# Revit family: O93 LED 130000 DALI 740 XNB_Unhosted
name_source: partatom
category: Lighting Fixtures
revit_build: Autodesk Revit 2016 (Build: 20161004_0715(x64)
units: mm (PartAtom-declared; Revit-internal decimal feet)

## family parameters
Always vertical = Yes
Cut with Voids When Loaded = No
Light Source = Yes
OmniClass Number = 23.80.70.00
OmniClass Title = Lighting
Part Type = Normal
Room Calculation Point = No
Round Connector Dimension = Use Diameter
Shared = No
Work Plane-Based = No

## types (1)
- O93 LED 130000 DALI 740 XNB_Unhosted
    #Ballast = 3
    Apparent Load = 867 VA
    ArticleNumber = 514084501
    Body Material and Colour = Default
    Color Filter = 16777215
    Description = O93 LED 130000 DALI 740 XNB
    Dimming Lamp Color Temperature Shift = Incandescent Lamp Curve
    EANNo = 8019455840118
    Emit Shape Visible in Rendering = Yes
    Emit from Rectangle Length = 565 mm
    Emit from Rectangle Width = 630 mm
    Expired = 0
    Frequency = 50 Hz
    FrequencyMax = 60 Hz
    Glamox Category = Outdoor
    Glamox Family = O93
    Glamox Mounting = Wall
    GlobalTradeItemNumber = 8019455840118
    Height = 398 mm
    Height2 = 40 mm
    IFC Classification = Light Fixture
    IPClass = 66
    IP_Code = 66
    Lamp = LED
    Length = 674 mm
    LightFixtureMountingType = OTHER
    LightFixturePlacingType = OTHER
    LumLength = 630 mm
    LumWidth = 565 mm
    MFArtNo = 514084501
    MaintenanceFactor = 0
    Manufacturer = Glamox
    Maximum TA = 35
    ModelLabel = O93 LED 130000 DALI 740 XNB
    ModelReference = O93
    NominalFrequencyRange = 50 Hz
    Number of Poles = 1
    Optic = XNB
    Photometric Web File = O93-LED-130000-DALI-740-XNB.ies
    Power Factor = 0.98
    PowerFactor = 98.00%
    RatedVoltage = 220 V
    Specification = Outdoor product, in Aluminium, for Wall/Facade/Pole mounting, impact classification IK8, IP66, light source LED, lumen out 126500lm, ballast type DALI, with light source type CRI>70, 4000K, optic type XNB = extra narrow beam.
    Termination = 5x6 SC
    Tilt Angle = 90.00°
    Total Load = 850 W
    TotalWattage = 850 W
    TypeOfBallast = DALI
    URL Denmark = http://glamox.com
    URL Estonia = http://glamox.com
    URL Finland = http://glamox.com
    URL Germany = http://glamox.com
    URL Ireland = http://glamox.com
    URL Norway = http://glamox.com
    URL Other = http://glamox.com
    URL Russia = http://glamox.com
    URL Sweden = http://glamox.com
    URL UK = http://glamox.com
    UpdateDate = 16.10.2020 07:02:09
    Voltage = 220 V
    VoltageMax = 240 V
    Width = 696 mm

## geometry (parser evidence)
native form markers: Blend x4
no freeform markers — native parametric forms only
